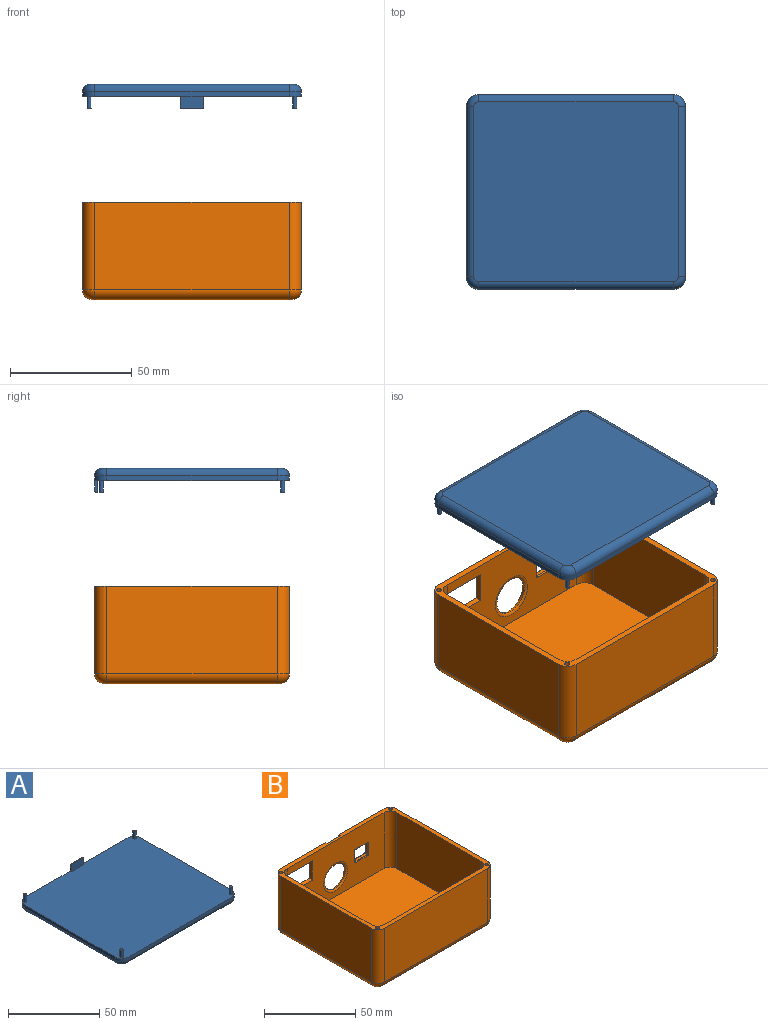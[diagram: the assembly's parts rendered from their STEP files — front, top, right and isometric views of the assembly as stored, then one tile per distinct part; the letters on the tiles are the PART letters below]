
ASSEMBLY  parts=2 mates=1
PART A: 30 faces, bbox 90x80x10 mm
  f0: plane 90x80mm, normal (0,0,1), area 7159.8mm2, adj f1,f2,f3,f4,f6,f7,f8,f9
  f1: plane 70x2mm, normal (1,0,0), area 140mm2, adj f0,f6,f9,f27
  f2: plane 80x6mm, normal (0,1,0), area 198.8mm2, adj f0,f6,f7,f19,f20,f26,f29
  f3: plane 70x2mm, normal (-1,0,0), area 140mm2, adj f0,f7,f8,f22
  f4: plane 80x2mm, normal (0,-1,0), area 160mm2, adj f0,f8,f9,f23
  f5: plane 84x74mm, normal (0,0,-1), area 6212.6mm2, adj f21,f22,f23,f24,f25,f26,f27,f28
  f6: cylinder r=5mm len=5mm, axis (0,0,1), area 15.7mm2, adj f0,f1,f2,f28
  f7: cylinder r=5mm len=5mm, axis (0,0,-1), area 15.7mm2, adj f0,f2,f3,f24
  f8: cylinder r=5mm len=5mm, axis (0,0,1), area 15.7mm2, adj f0,f3,f4,f21
  f9: cylinder r=5mm len=5mm, axis (0,0,-1), area 15.7mm2, adj f0,f1,f4,f25
  f10: cylinder r=0.85mm len=4.8mm, axis (0,0,-1), area 25.6mm2, adj f0,f11
  f11: plane 1.7x1.7mm, normal (0,0,1), area 2.3mm2, adj f10
  f12: cylinder r=0.85mm len=4.8mm, axis (0,0,-1), area 25.6mm2, adj f0,f13
  f13: plane 1.7x1.7mm, normal (0,0,1), area 2.3mm2, adj f12
  f14: cylinder r=0.85mm len=4.8mm, axis (0,0,-1), area 25.6mm2, adj f0,f15
  f15: plane 1.7x1.7mm, normal (0,0,1), area 2.3mm2, adj f14
  f16: cylinder r=0.85mm len=4.8mm, axis (0,0,-1), area 25.6mm2, adj f0,f17
  f17: plane 1.7x1.7mm, normal (0,0,1), area 2.3mm2, adj f16
  f18: plane 9.7x5mm, normal (0,-1,0), area 48.5mm2, adj f0,f19,f20,f29
  f19: plane 5x1mm, normal (1,0,0), area 4.8mm2, adj f0,f2,f18,f29
  f20: plane 5x1mm, normal (-1,0,0), area 4.8mm2, adj f0,f2,f18,f29
  f21: torus R=2mm, axis (0,0,1), area 28.9mm2, adj f5,f8,f22,f23
  f22: cylinder r=3mm len=70mm, axis (0,-1,0), area 329.9mm2, adj f3,f5,f21,f24
  f23: cylinder r=3mm len=80mm, axis (1,0,0), area 377mm2, adj f4,f5,f21,f25
  f24: torus R=2mm, axis (0,0,1), area 28.9mm2, adj f5,f7,f22,f26
  f25: torus R=2mm, axis (0,0,1), area 28.9mm2, adj f5,f9,f23,f27
  f26: cylinder r=3mm len=80mm, axis (-1,0,0), area 377mm2, adj f2,f5,f24,f28
  f27: cylinder r=3mm len=70mm, axis (0,1,0), area 329.9mm2, adj f1,f5,f25,f28
  f28: torus R=2mm, axis (0,0,1), area 28.9mm2, adj f5,f6,f26,f27
  f29: cylinder r=1mm len=9.7mm, axis (1,0,0), area 15.2mm2, adj f2,f18,f19,f20
PART B: 70 faces, bbox 90x80x40 mm
  f0: plane 80x36mm, normal (0,1,0), area 2003.8mm2, adj f3,f15,f16,f28,f29,f30,f36,f43
  f1: plane 75x37.5mm, normal (0,-1,0), area 2085.5mm2, adj f2,f3,f11,f14,f51,f52,f55,f56
  f2: cylinder r=5mm len=37.5mm, axis (0,0,1), area 286.4mm2, adj f1,f3,f9,f11,f63,f64,f65,f67
  f3: plane 90x80mm, normal (0,0,1), area 802.4mm2, adj f0,f1,f2,f4,f5,f6,f8,f9
  f4: plane 70x36mm, normal (1,0,0), area 2520mm2, adj f3,f15,f18,f37
  f5: plane 70x36mm, normal (-1,0,0), area 2520mm2, adj f3,f16,f17,f32
  f6: plane 80x36mm, normal (0,-1,0), area 2880mm2, adj f3,f17,f18,f33
  f7: plane 82x72mm, normal (0,0,-1), area 5903.1mm2, adj f31,f32,f33,f34,f35,f36,f37,f38
  f8: plane 65x37.5mm, normal (-1,0,0), area 2437.5mm2, adj f3,f11,f13,f14
  f9: plane 65x37.5mm, normal (1,0,0), area 2437.5mm2, adj f2,f3,f11,f12
  f10: plane 75x37.5mm, normal (0,1,0), area 2812.5mm2, adj f3,f11,f12,f13
  f11: plane 85x75mm, normal (0,0,1), area 6353.5mm2, adj f1,f2,f8,f9,f10,f12,f13,f14
  f12: cylinder r=5mm len=37.5mm, axis (0,0,-1), area 294.5mm2, adj f3,f9,f10,f11
  f13: cylinder r=5mm len=37.5mm, axis (0,0,1), area 294.5mm2, adj f3,f8,f10,f11
  f14: cylinder r=5mm len=37.5mm, axis (0,0,-1), area 294.5mm2, adj f1,f3,f8,f11
  f15: cylinder r=5mm len=36mm, axis (0,0,1), area 282.7mm2, adj f0,f3,f4,f38
  f16: cylinder r=5mm len=36mm, axis (0,0,-1), area 282.7mm2, adj f0,f3,f5,f34
  f17: cylinder r=5mm len=36mm, axis (0,0,1), area 282.7mm2, adj f3,f5,f6,f31
  f18: cylinder r=5mm len=36mm, axis (0,0,-1), area 282.7mm2, adj f3,f4,f6,f35
  f19: cylinder r=1mm len=5mm, axis (0,0,1), area 31.4mm2, adj f3,f20
  f20: plane 2x2mm, normal (0,0,1), area 3.1mm2, adj f19
  f21: cylinder r=1mm len=5mm, axis (0,0,1), area 31.4mm2, adj f3,f22
  f22: plane 2x2mm, normal (0,0,1), area 3.1mm2, adj f21
  f23: cylinder r=1mm len=5mm, axis (0,0,1), area 31.4mm2, adj f3,f24
  f24: plane 2x2mm, normal (0,0,1), area 3.1mm2, adj f23
  f25: cylinder r=1mm len=5mm, axis (0,0,1), area 31.4mm2, adj f3,f26
  f26: plane 2x2mm, normal (0,0,1), area 3.1mm2, adj f25
  f27: plane 10x10mm, normal (0,1,0), area 100mm2, adj f3,f28,f29,f30
  f28: plane 10x1mm, normal (-1,0,0), area 10mm2, adj f0,f3,f27,f30
  f29: plane 10x1mm, normal (1,0,0), area 10mm2, adj f0,f3,f27,f30
  f30: plane 10x1mm, normal (0,0,1), area 10mm2, adj f0,f27,f28,f29
  f31: torus R=1mm, axis (0,0,1), area 35mm2, adj f7,f17,f32,f33
  f32: cylinder r=4mm len=70mm, axis (0,-1,0), area 439.8mm2, adj f5,f7,f31,f34
  f33: cylinder r=4mm len=80mm, axis (1,0,0), area 502.7mm2, adj f6,f7,f31,f35
  f34: torus R=1mm, axis (0,0,1), area 35mm2, adj f7,f16,f32,f36
  f35: torus R=1mm, axis (0,0,1), area 35mm2, adj f7,f18,f33,f37
  f36: cylinder r=4mm len=80mm, axis (-1,0,0), area 502.7mm2, adj f0,f7,f34,f38
  f37: cylinder r=4mm len=70mm, axis (0,1,0), area 439.8mm2, adj f4,f7,f35,f38
  f38: torus R=1mm, axis (0,0,1), area 35mm2, adj f7,f15,f36,f37
  f39: plane 9x1.5mm, normal (0,0,1), area 13.5mm2, adj f43,f46,f50,f51
  f40: plane 7x1.5mm, normal (1,0,0), area 10.5mm2, adj f49,f50,f58,f59
  f41: plane 9x1.5mm, normal (0,0,-1), area 13.5mm2, adj f48,f57,f58,f62
  f42: plane 7x1.5mm, normal (-1,0,0), area 10.5mm2, adj f46,f47,f56,f57
  f43: cylinder r=0.5mm len=9mm, axis (-1,0,0), area 7.1mm2, adj f0,f39,f44,f45
  f44: torus R=1mm, axis (0,-1,0), area 0.8mm2, adj f0,f43,f46,f47
  f45: torus R=1mm, axis (0,-1,0), area 0.8mm2, adj f0,f43,f49,f50
  f46: cylinder r=0.5mm len=1.5mm, axis (0,-1,0), area 1.2mm2, adj f39,f42,f44,f52
  f47: cylinder r=0.5mm len=7mm, axis (0,0,-1), area 5.5mm2, adj f0,f42,f44,f53
  f48: cylinder r=0.5mm len=9mm, axis (1,0,0), area 7.1mm2, adj f0,f41,f53,f54
  f49: cylinder r=0.5mm len=7mm, axis (0,0,1), area 5.5mm2, adj f0,f40,f45,f54
  f50: cylinder r=0.5mm len=1.5mm, axis (0,1,0), area 1.2mm2, adj f39,f40,f45,f55
  f51: cylinder r=0.5mm len=9mm, axis (-1,0,0), area 7.1mm2, adj f1,f39,f52,f55
  f52: torus R=1mm, axis (0,-1,0), area 0.8mm2, adj f1,f46,f51,f56
  f53: torus R=1mm, axis (0,-1,0), area 0.8mm2, adj f0,f47,f48,f57
  f54: torus R=1mm, axis (0,-1,0), area 0.8mm2, adj f0,f48,f49,f58
  f55: torus R=1mm, axis (0,-1,0), area 0.8mm2, adj f1,f50,f51,f59
  f56: cylinder r=0.5mm len=7mm, axis (0,0,-1), area 5.5mm2, adj f1,f42,f52,f60
  f57: cylinder r=0.5mm len=1.5mm, axis (0,1,0), area 1.2mm2, adj f41,f42,f53,f60
  f58: cylinder r=0.5mm len=1.5mm, axis (0,-1,0), area 1.2mm2, adj f40,f41,f54,f61
  f59: cylinder r=0.5mm len=7mm, axis (0,0,1), area 5.5mm2, adj f1,f40,f55,f61
  f60: torus R=1mm, axis (0,-1,0), area 0.8mm2, adj f1,f56,f57,f62
  f61: torus R=1mm, axis (0,-1,0), area 0.8mm2, adj f1,f58,f59,f62
  f62: cylinder r=0.5mm len=9mm, axis (1,0,0), area 7.1mm2, adj f1,f41,f60,f61
  f63: plane 13x2.53mm, normal (1,0,0), area 32.8mm2, adj f0,f2,f64,f65
  f64: plane 20x2.53mm, normal (0,0,1), area 50mm2, adj f0,f1,f2,f63,f66
  f65: plane 20x2.53mm, normal (0,0,-1), area 50mm2, adj f0,f1,f2,f63,f66
  f66: plane 13x2.5mm, normal (-1,0,0), area 32.5mm2, adj f0,f1,f64,f65
  f67: cylinder r=5.75mm len=11.5mm, axis (0,1,0), area 90.3mm2, adj f0,f1,f2
  f68: torus R=10mm, axis (0,-1,0), area 172.3mm2, adj f0,f69
  f69: torus R=9.32mm, axis (0,-1,0), area 78.4mm2, adj f1,f68
PLACE A rot(axis=(0,1,0),180deg) t=(0,0,88.5)mm
PLACE B at identity
MATE slider A.f0 <-> B.f3  axis (0,0,-1) through (0,-40,83.5)mm
